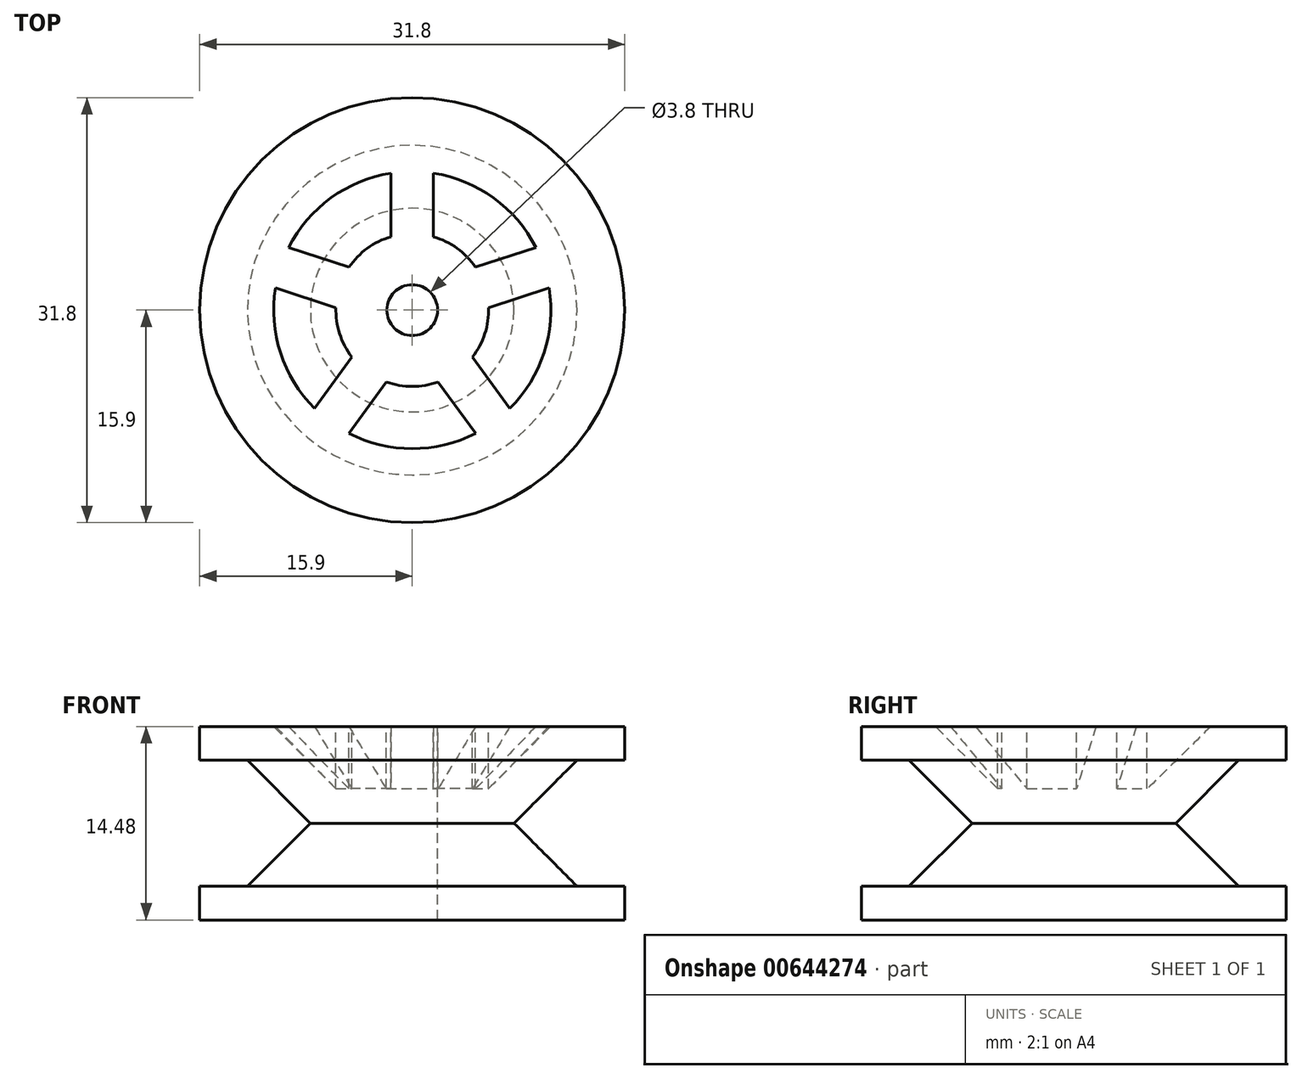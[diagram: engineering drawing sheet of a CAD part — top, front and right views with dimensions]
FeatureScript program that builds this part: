
annotation { "Feature Type Name" : "Feature", "Feature Type Description" : "" }
export const myFeature = defineFeature(function(context is Context, id is Id, definition is map)
    precondition{}
    {
        {
            var Q0;
            Q0=qCreatedBy(makeId("Top.planeOp"),FACE);
            var sketch = newSketch(context, id + "F0", { "sketchPlane" : qUnion([Q0])});
            skCircle(sketch, "E0", {"center": v(0, 0) * mm, "radius": 15.9 * mm});
            skSolve(sketch);
        }
        {
            var Q0;
            Q0=makeQuery(id+"F0.imprint","IMPRINT",FACE,{"disambiguationData":[TD([[makeQuery(id+"F0.imprint","IMPRINT",EDGE,{"derivedFrom":sQuery(id+"F0.wireOp",EDGE,"E0")}),1.0]])]});
            var Q1;
            Q1 = qSketchRegion(id + "F2", true);
            extrude(context, id + "F1", {"entities" : qUnion([Q0, Q1]), "endBound" : BoundingType.SYMMETRIC, "depth" : 14.48 * mm, "offsetDistance" : 25.4 * mm});
        }
        {
            var Q0;
            Q0=makeQuery(id+"F1.opExtrude","CAP_FACE",FACE,{"disambiguationData":[OSD([sQuery(id+"F0.wireOp",EDGE,"E0")])],"isStart":false});
            var sketch = newSketch(context, id + "F2", { "sketchPlane" : qUnion([Q0])});
            skCircle(sketch, "E1", {"center": v(0, 0) * mm, "radius": 1.9 * mm});
            skSolve(sketch);
        }
        {
            var Q0;
            Q0 = qSketchRegion(id + "F2", true);
            extrude(context, id + "F3", {"entities" : qUnion([Q0]), "operationType" : NewBodyOperationType.REMOVE, "endBound" : BoundingType.THROUGH_ALL, "oppositeDirection" : true, "depth" : 25.4 * mm, "offsetDistance" : 25.4 * mm});
        }
        {
            var Q0;
            Q0=qCreatedBy(makeId("Right.planeOp"),FACE);
            var sketch = newSketch(context, id + "F4", { "sketchPlane" : qUnion([Q0])});
            skLineSegment(sketch, "E2", {"start": v(18.62, 4.71) * mm, "end": v(12.33, 4.71) * mm});
            skLineSegment(sketch, "E3", {"start": v(12.33, 4.71) * mm, "end": v(7.62, 0) * mm});
            skLineSegment(sketch, "E4", {"start": v(7.62, 0) * mm, "end": v(12.33, -4.71) * mm});
            skLineSegment(sketch, "E5", {"start": v(12.33, -4.71) * mm, "end": v(18.62, -4.71) * mm});
            skLineSegment(sketch, "E6", {"start": v(18.62, -4.71) * mm, "end": v(18.62, 4.71) * mm});
            skLineSegment(sketch, "E7", {"start": v(0, 0) * mm, "end": v(0, 16.3) * mm, "construction": true});
            skLineSegment(sketch, "E8", {"start": v(12, 8.88) * mm, "end": v(5.71, 2.59) * mm});
            skLineSegment(sketch, "E9", {"start": v(5.72, 2.59) * mm, "end": v(5.72, 8.88) * mm});
            skLineSegment(sketch, "E10", {"start": v(5.72, 8.88) * mm, "end": v(12, 8.88) * mm});
            skSolve(sketch);
        }
        {
            var Q0;
            Q0 = qSketchRegion(id + "F4", true);
            var Q1;
            Q1=sQuery(id+"F4.wireOp",EDGE,"E7");
            revolve(context, id + "F5", {"operationType" : NewBodyOperationType.REMOVE, "entities" : qUnion([Q0]), "axis" : qUnion([Q1]), "revolveType" : RevolveType.FULL, "oppositeDirection" : true});
        }
        {
            var Q0;
            {var subQ0=sQuery(id+"F0.wireOp",EDGE,"E0");Q0=makeQuery(id+"F5.boolean.opBoolean","SPLIT",FACE,{"disambiguationData":[TD([makeQuery(id+"F1.opExtrude","SWEPT_FACE",FACE,{"disambiguationData":[OSD([subQ0])]})])],"derivedFrom":makeQuery(id+"F1.opExtrude","CAP_FACE",FACE,{"disambiguationData":[OSD([subQ0])],"isStart":false})});}
            var sketch = newSketch(context, id + "F6", { "sketchPlane" : qUnion([Q0])});
            skLineSegment(sketch, "E11.bottom", {"start": v(-1.59, 11.46) * mm, "end": v(1.59, 11.46) * mm});
            skLineSegment(sketch, "E11.top", {"start": v(-1.59, 3.95) * mm, "end": v(1.59, 3.95) * mm});
            skLineSegment(sketch, "E11.left", {"start": v(-1.59, 11.46) * mm, "end": v(-1.59, 3.95) * mm});
            skLineSegment(sketch, "E11.right", {"start": v(1.59, 11.46) * mm, "end": v(1.59, 3.95) * mm});
            skPoint(sketch, "E11.middle", {"position": v(0, 7.7) * mm});
            skLineSegment(sketch, "E12.1.0", {"start": v(-11.39, 2.03) * mm, "end": v(-4.25, -0.29) * mm});
            skLineSegment(sketch, "E12.1.1", {"start": v(-11.39, 2.03) * mm, "end": v(-10.4, 5.05) * mm});
            skLineSegment(sketch, "E12.1.2", {"start": v(-10.4, 5.05) * mm, "end": v(-3.27, 2.73) * mm});
            skLineSegment(sketch, "E12.1.3", {"start": v(-4.25, -0.29) * mm, "end": v(-3.27, 2.73) * mm});
            skLineSegment(sketch, "E12.2.0", {"start": v(-5.45, -10.2) * mm, "end": v(-1.04, -4.13) * mm});
            skLineSegment(sketch, "E12.2.1", {"start": v(-5.45, -10.2) * mm, "end": v(-8.02, -8.34) * mm});
            skLineSegment(sketch, "E12.2.2", {"start": v(-8.02, -8.34) * mm, "end": v(-3.6, -2.26) * mm});
            skLineSegment(sketch, "E12.2.3", {"start": v(-1.04, -4.13) * mm, "end": v(-3.6, -2.26) * mm});
            skPoint(sketch, "E12.center", {"position": v(0, 0) * mm});
            skLineSegment(sketch, "E13.2.3.0", {"start": v(8.02, -8.34) * mm, "end": v(3.6, -2.26) * mm});
            skLineSegment(sketch, "E13.3.3.0", {"start": v(8.02, -8.34) * mm, "end": v(5.45, -10.2) * mm});
            skLineSegment(sketch, "E13.6.3.0", {"start": v(5.45, -10.2) * mm, "end": v(1.04, -4.13) * mm});
            skLineSegment(sketch, "E13.9.3.0", {"start": v(3.6, -2.26) * mm, "end": v(1.04, -4.13) * mm});
            skLineSegment(sketch, "E13.2.4.0", {"start": v(10.4, 5.05) * mm, "end": v(3.27, 2.73) * mm});
            skLineSegment(sketch, "E13.3.4.0", {"start": v(10.4, 5.05) * mm, "end": v(11.39, 2.03) * mm});
            skLineSegment(sketch, "E13.6.4.0", {"start": v(11.39, 2.03) * mm, "end": v(4.25, -0.29) * mm});
            skLineSegment(sketch, "E13.9.4.0", {"start": v(3.27, 2.73) * mm, "end": v(4.25, -0.29) * mm});
            skSolve(sketch);
        }
        {
            var Q0;
            Q0 = qSketchRegion(id + "F6", true);
            var Q1;
            Q1=makeQuery(id+"F5.boolean.opBoolean","COPY",FACE,{"derivedFrom":makeQuery(id+"F5.opRevolve","SWEPT_FACE",FACE,{"disambiguationData":[OSD([sQuery(id+"F4.wireOp",EDGE,"E8")])]})});
            extrude(context, id + "F7", {"entities" : qUnion([Q0]), "operationType" : NewBodyOperationType.ADD, "endBound" : BoundingType.UP_TO_SURFACE, "oppositeDirection" : true, "depth" : 25.4 * mm, "endBoundEntityFace" : qUnion([Q1]), "offsetDistance" : 25.4 * mm});
        }
    });
